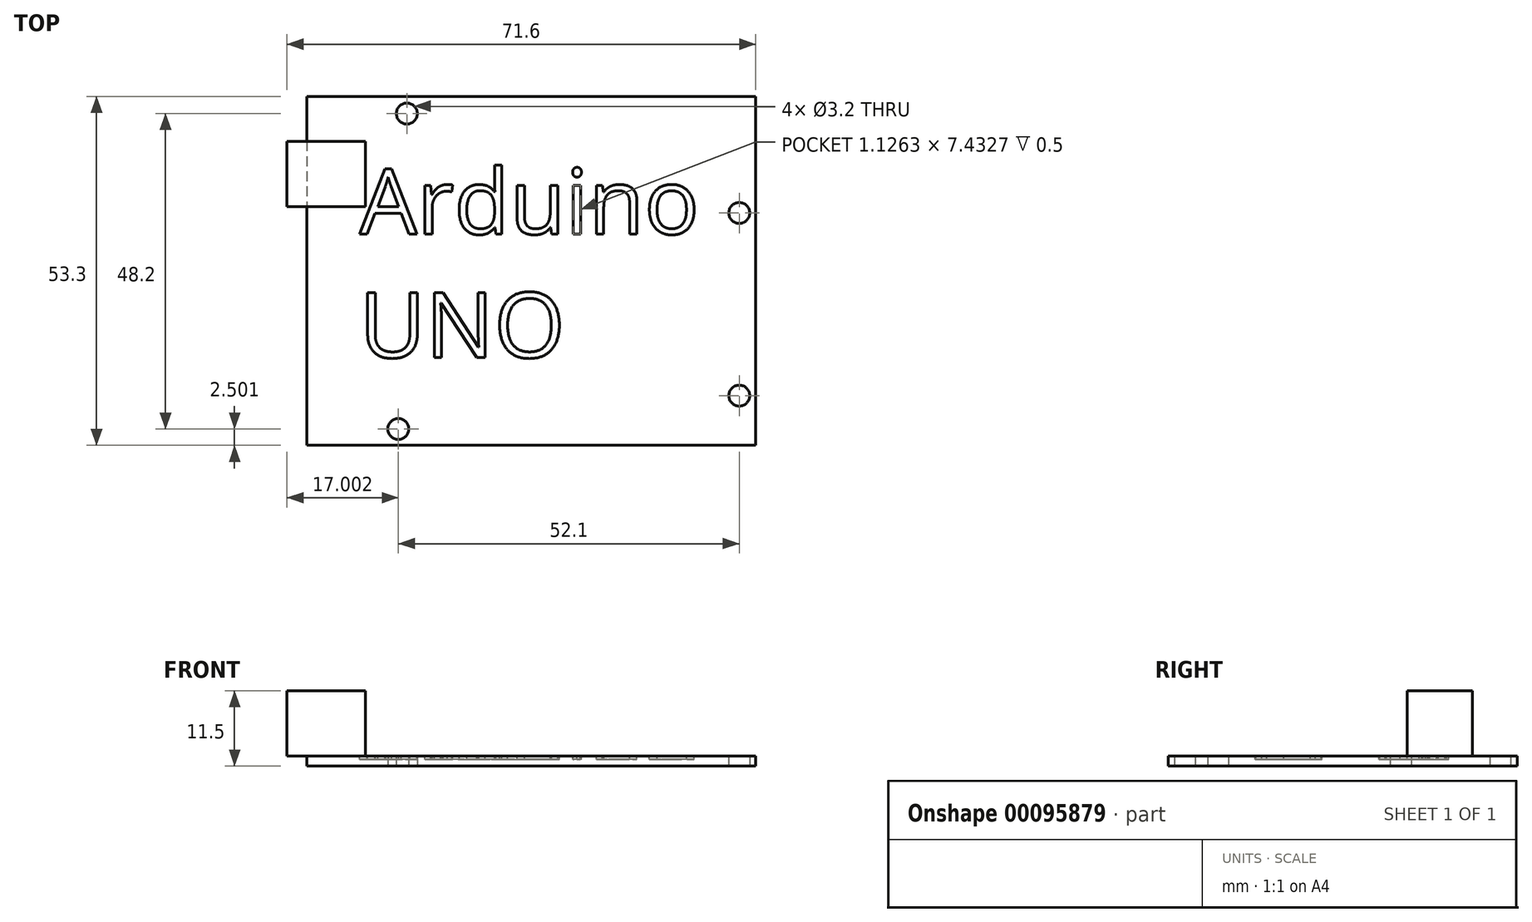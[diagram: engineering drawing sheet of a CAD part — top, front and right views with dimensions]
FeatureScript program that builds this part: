
annotation { "Feature Type Name" : "Feature", "Feature Type Description" : "" }
export const myFeature = defineFeature(function(context is Context, id is Id, definition is map)
    precondition{}
    {
        {
            var Q0;
            Q0=qCreatedBy(makeId("Top.planeOp"),FACE);
            var sketch = newSketch(context, id + "F0", { "sketchPlane" : qUnion([Q0])});
            skLineSegment(sketch, "E0.bottom", {"start": v(-0.1, 35.9) * mm, "end": v(68.5, 35.9) * mm});
            skLineSegment(sketch, "E0.top", {"start": v(-0.1, -17.4) * mm, "end": v(68.5, -17.4) * mm});
            skLineSegment(sketch, "E0.left", {"start": v(-0.1, 35.9) * mm, "end": v(-0.1, -17.4) * mm});
            skLineSegment(sketch, "E0.right", {"start": v(68.5, 35.9) * mm, "end": v(68.5, -17.4) * mm});
            skCircle(sketch, "E1", {"center": v(13.9, -14.9) * mm, "radius": 1.6 * mm});
            skCircle(sketch, "E2", {"center": v(15.2, 33.3) * mm, "radius": 1.6 * mm});
            skCircle(sketch, "E3", {"center": v(66, 18.1) * mm, "radius": 1.6 * mm});
            skCircle(sketch, "E4", {"center": v(66, -9.8) * mm, "radius": 1.6 * mm});
            skSolve(sketch);
        }
        {
            var Q0;
            Q0=makeQuery(id+"F0.imprint","IMPRINT",FACE,{"disambiguationData":[TD([[makeQuery(id+"F0.imprint","IMPRINT",EDGE,{"derivedFrom":sQuery(id+"F0.wireOp",EDGE,"E0.bottom")}),-1.0]])]});
            extrude(context, id + "F1", {"entities" : qUnion([Q0]), "depth" : 1.5 * mm});
        }
        {
            var Q0;
            Q0=makeQuery(id+"F1.opExtrude","CAP_FACE",FACE,{"disambiguationData":[OSD([sQuery(id+"F0.wireOp",EDGE,"E0.bottom"),sQuery(id+"F0.wireOp",EDGE,"E0.top"),sQuery(id+"F0.wireOp",EDGE,"E0.left"),sQuery(id+"F0.wireOp",EDGE,"E0.right"),sQuery(id+"F0.wireOp",EDGE,"E1"),sQuery(id+"F0.wireOp",EDGE,"E2"),sQuery(id+"F0.wireOp",EDGE,"E3"),sQuery(id+"F0.wireOp",EDGE,"E4")])],"isStart":false});
            var sketch = newSketch(context, id + "F2", { "sketchPlane" : qUnion([Q0])});
            skText(sketch, "E5", { "text": "Arduino\nUNO", "fontName": "OpenSans-Regular.ttf"});
            const initialGuessF2  = {"E5": [0.00795, 0.01488, 1, 0, 0.01]};
            skSetInitialGuess(sketch, initialGuessF2);
            skSolve(sketch);
        }
        {
            var Q0;
            Q0 = qSketchRegion(id + "F2", true);
            extrude(context, id + "F3", {"entities" : qUnion([Q0]), "operationType" : NewBodyOperationType.REMOVE, "oppositeDirection" : true, "depth" : 0.5 * mm});
        }
        {
            var Q0;
            {var subQ0=sQuery(id+"F0.wireOp",EDGE,"E4");var subQ1=sQuery(id+"F0.wireOp",EDGE,"E0.left");var subQ2=sQuery(id+"F0.wireOp",EDGE,"E0.bottom");var subQ3=sQuery(id+"F0.wireOp",EDGE,"E0.right");var subQ4=sQuery(id+"F0.wireOp",EDGE,"E0.top");var subQ5=sQuery(id+"F0.wireOp",EDGE,"E2");var subQ6=sQuery(id+"F0.wireOp",EDGE,"E1");var subQ7=sQuery(id+"F0.wireOp",EDGE,"E3");Q0=makeQuery(id+"F3.boolean.opBoolean","SPLIT",FACE,{"disambiguationData":[TD([makeQuery(id+"F1.opExtrude","SWEPT_FACE",FACE,{"disambiguationData":[OSD([subQ2])]})])],"derivedFrom":makeQuery(id+"F1.opExtrude","CAP_FACE",FACE,{"disambiguationData":[OSD([subQ2,subQ4,subQ1,subQ3,subQ6,subQ5,subQ7,subQ0])],"isStart":false})});}
            var sketch = newSketch(context, id + "F4", { "sketchPlane" : qUnion([Q0])});
            skLineSegment(sketch, "E6.bottom", {"start": v(-0.1, 29.05) * mm, "end": v(8.9, 29.05) * mm});
            skLineSegment(sketch, "E6.top", {"start": v(-0.1, 19.05) * mm, "end": v(8.9, 19.05) * mm});
            skLineSegment(sketch, "E6.left", {"start": v(-0.1, 29.05) * mm, "end": v(-0.1, 19.05) * mm});
            skLineSegment(sketch, "E6.right", {"start": v(8.9, 29.05) * mm, "end": v(8.9, 19.05) * mm});
            skLineSegment(sketch, "E7.bottom", {"start": v(-0.1, 29.05) * mm, "end": v(-3.1, 29.05) * mm});
            skLineSegment(sketch, "E7.top", {"start": v(-0.1, 19.05) * mm, "end": v(-3.1, 19.05) * mm});
            skLineSegment(sketch, "E7.right", {"start": v(-3.1, 29.05) * mm, "end": v(-3.1, 19.05) * mm});
            skSolve(sketch);
        }
        {
            var Q0;
            Q0 = qSketchRegion(id + "F4", true);
            extrude(context, id + "F5", {"entities" : qUnion([Q0]), "operationType" : NewBodyOperationType.ADD, "depth" : 10 * mm});
        }
    });
